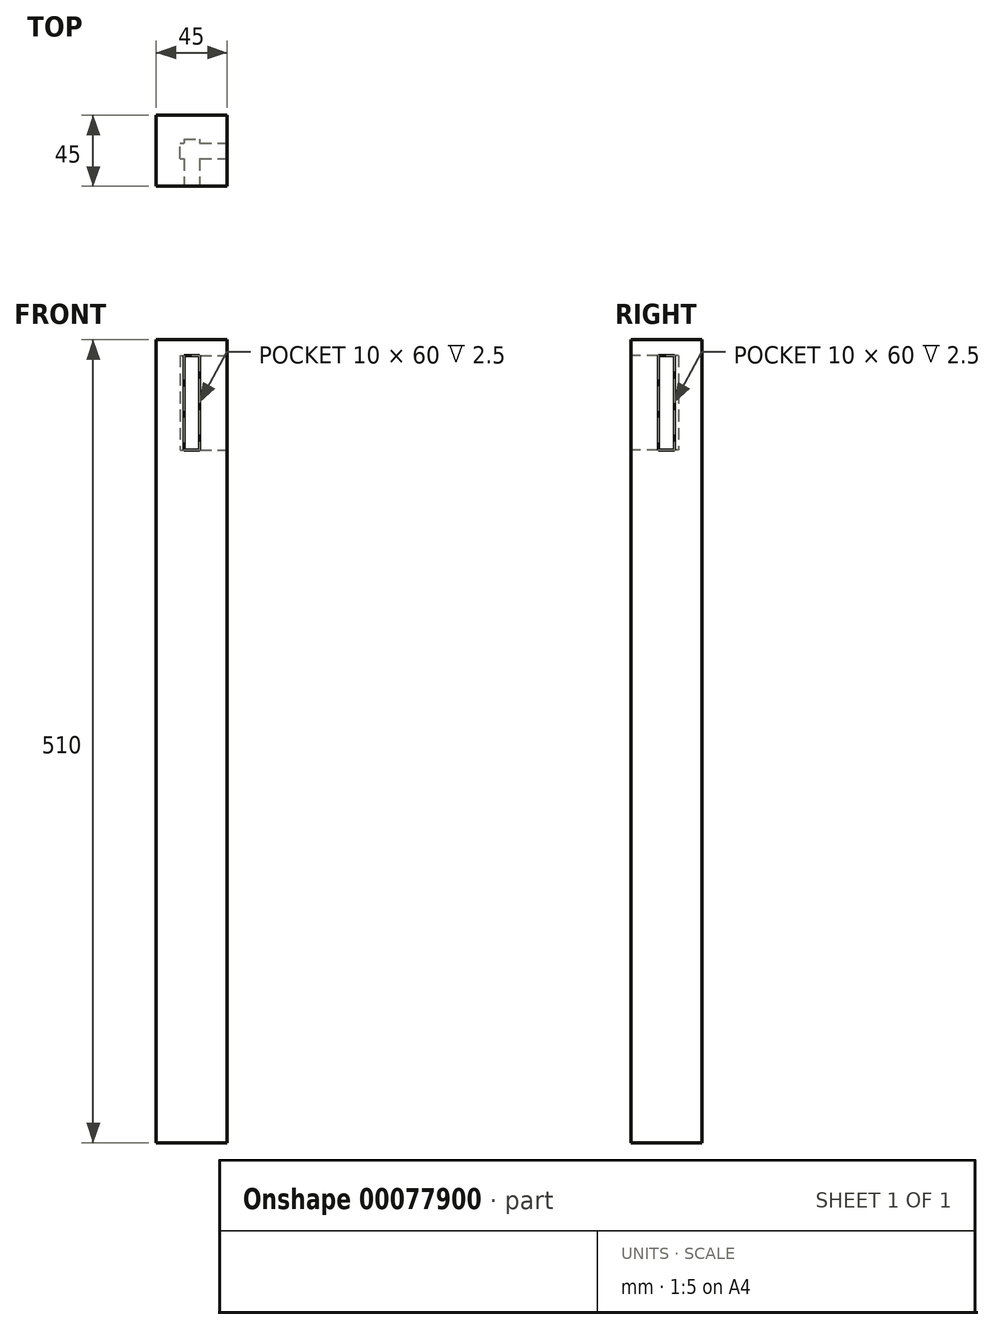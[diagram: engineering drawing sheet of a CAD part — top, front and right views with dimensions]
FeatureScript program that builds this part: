
annotation { "Feature Type Name" : "Feature", "Feature Type Description" : "" }
export const myFeature = defineFeature(function(context is Context, id is Id, definition is map)
    precondition{}
    {
        {
            var Q0;
            Q0=qCreatedBy(makeId("Top.planeOp"),FACE);
            var sketch = newSketch(context, id + "F0", { "sketchPlane" : qUnion([Q0])});
            skLineSegment(sketch, "E0.bottom", {"start": v(0, 0) * mm, "end": v(-45, 0) * mm});
            skLineSegment(sketch, "E0.top", {"start": v(0, 45) * mm, "end": v(-45, 45) * mm});
            skLineSegment(sketch, "E0.left", {"start": v(0, 0) * mm, "end": v(0, 45) * mm});
            skLineSegment(sketch, "E0.right", {"start": v(-45, 0) * mm, "end": v(-45, 45) * mm});
            skSolve(sketch);
        }
        {
            var Q0;
            Q0=qSketchRegion(id+"F0",true);
            extrude(context, id + "F1", {"entities" : qUnion([Q0]), "depth" : 510 * mm});
        }
        {
            var Q0;
            Q0=makeQuery(id+"F1.opExtrude","SWEPT_FACE",FACE,{"disambiguationData":[OSD([sQuery(id+"F0.wireOp",EDGE,"E0.left")])]});
            var sketch = newSketch(context, id + "F2", { "sketchPlane" : qUnion([Q0])});
            skLineSegment(sketch, "E1.bottom", {"start": v(17.5, 500) * mm, "end": v(27.5, 500) * mm});
            skLineSegment(sketch, "E1.top", {"start": v(17.5, 440) * mm, "end": v(27.5, 440) * mm});
            skLineSegment(sketch, "E1.left", {"start": v(17.5, 500) * mm, "end": v(17.5, 440) * mm});
            skLineSegment(sketch, "E1.right", {"start": v(27.5, 500) * mm, "end": v(27.5, 440) * mm});
            skLineSegment(sketch, "E2", {"start": v(22.5, 500) * mm, "end": v(22.5, 440) * mm, "construction": true});
            skLineSegment(sketch, "E3", {"start": v(0, 500) * mm, "end": v(45, 500) * mm, "construction": true});
            skSolve(sketch);
        }
        {
            var Q0;
            Q0=makeQuery(id+"F1.opExtrude","SWEPT_FACE",FACE,{"disambiguationData":[OSD([sQuery(id+"F0.wireOp",EDGE,"E0.bottom")])]});
            var sketch = newSketch(context, id + "F3", { "sketchPlane" : qUnion([Q0])});
            skLineSegment(sketch, "E4.bottom", {"start": v(-27.5, 500) * mm, "end": v(-17.5, 500) * mm});
            skLineSegment(sketch, "E4.top", {"start": v(-27.5, 440) * mm, "end": v(-17.5, 440) * mm});
            skLineSegment(sketch, "E4.left", {"start": v(-27.5, 500) * mm, "end": v(-27.5, 440) * mm});
            skLineSegment(sketch, "E4.right", {"start": v(-17.5, 500) * mm, "end": v(-17.5, 440) * mm});
            skLineSegment(sketch, "E5", {"start": v(-22.5, 500) * mm, "end": v(-22.5, 440) * mm, "construction": true});
            skLineSegment(sketch, "E6", {"start": v(-45, 500) * mm, "end": v(0, 500) * mm, "construction": true});
            skLineSegment(sketch, "E7.0.left", {"start": v(-17.5, 500) * mm, "end": v(-17.5, 440) * mm, "construction": true});
            skLineSegment(sketch, "E7.0.right", {"start": v(-27.5, 500) * mm, "end": v(-27.5, 440) * mm, "construction": true});
            skSolve(sketch);
        }
        {
            var Q0;
            Q0=makeQuery(id+"F2.imprint","IMPRINT",FACE,{"disambiguationData":[TD([[makeQuery(id+"F2.imprint","IMPRINT",EDGE,{"derivedFrom":sQuery(id+"F2.wireOp",EDGE,"E1.bottom")}),-1.0]])]});
            extrude(context, id + "F4", {"entities" : qUnion([Q0]), "operationType" : NewBodyOperationType.REMOVE, "oppositeDirection" : true, "depth" : 30 * mm});
        }
        {
            var Q0;
            Q0=makeQuery(id+"F3.imprint","IMPRINT",FACE,{"disambiguationData":[TD([[makeQuery(id+"F3.imprint","IMPRINT",EDGE,{"derivedFrom":sQuery(id+"F3.wireOp",EDGE,"E4.bottom")}),-1.0]])]});
            extrude(context, id + "F5", {"entities" : qUnion([Q0]), "operationType" : NewBodyOperationType.REMOVE, "oppositeDirection" : true, "depth" : 30 * mm});
        }
    });
